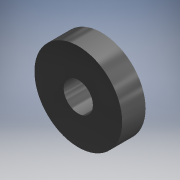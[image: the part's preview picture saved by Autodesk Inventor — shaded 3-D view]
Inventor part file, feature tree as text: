
AUTODESK INVENTOR PART (.ipt)
format: ipt  version: 2019 (Build 230136000, 136)  size: 90,112 bytes
history: native  units: mm (DEFAULTED — no unit token found)
features: extrude x1, sketch x1
ambient origin geometry x8: Origin, YZ Plane, XZ Plane, XY Plane, X Axis, Y Axis, Z Axis, Center Point
bodies: Solid1 (feature_tree)
feature tree (2):
  extrude  "Extrusion1"  Depth=5.08mm
  sketch  "Sketch1"  dims[d0=6.35mm d1=19.05mm d2=5.08mm d3=0.0mm]
